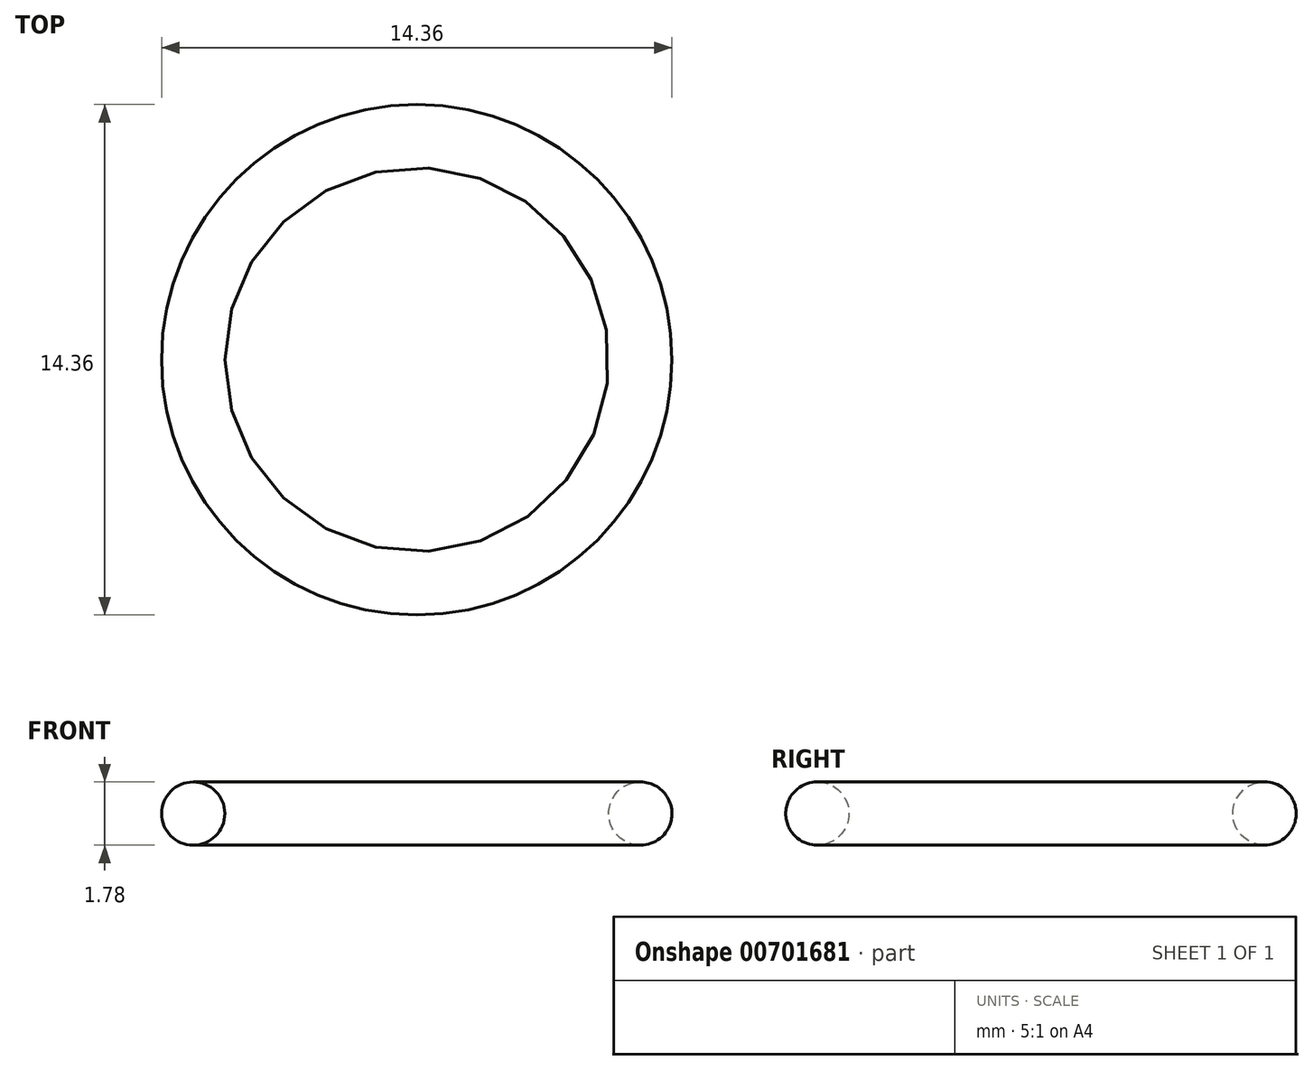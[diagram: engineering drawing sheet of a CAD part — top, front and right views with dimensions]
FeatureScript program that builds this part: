
annotation { "Feature Type Name" : "Feature", "Feature Type Description" : "" }
export const myFeature = defineFeature(function(context is Context, id is Id, definition is map)
    precondition{}
    {
        {
            var Q0;
            Q0=qCreatedBy(makeId("Right.planeOp"),FACE);
            var sketch = newSketch(context, id + "F0", { "sketchPlane" : qUnion([Q0])});
            skCircle(sketch, "E0", {"center": v(-6.3, 0) * mm, "radius": 0.89 * mm});
            skLineSegment(sketch, "E1", {"start": v(0, 0) * mm, "end": v(0, 13.43) * mm, "construction": true});
            skSolve(sketch);
        }
        {
            var Q0;
            Q0=makeQuery(id+"F0.imprint","IMPRINT",FACE,{"disambiguationData":[TD([[makeQuery(id+"F0.imprint","IMPRINT",EDGE,{"derivedFrom":sQuery(id+"F0.wireOp",EDGE,"E0")}),1.0]])]});
            var Q1;
            Q1=sQuery(id+"F0.wireOp",EDGE,"E1");
            revolve(context, id + "F1", {"entities" : qUnion([Q0]), "axis" : qUnion([Q1]), "revolveType" : RevolveType.FULL});
        }
    });
